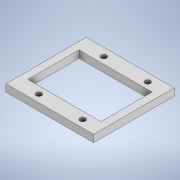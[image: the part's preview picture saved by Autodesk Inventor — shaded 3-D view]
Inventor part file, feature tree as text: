
AUTODESK INVENTOR PART (.ipt)
format: ipt  version: 2022 (Build 260153000, 153)  size: 117,760 bytes
history: native  units: mm
features: extrude x1, sketch x1
ambient origin geometry x8: Origin, YZ Plane, XZ Plane, XY Plane, X Axis, Y Axis, Z Axis, Center Point
bodies: Solid1 (feature_tree)
feature tree (2):
  extrude  "Extrusion1"  Depth=11.0mm
  sketch  "Sketch1"  dims[d0=12.0mm d1=11.0mm d2=5.5mm d3=7.5mm d4=10.0mm d5=7.0mm d6=2.0mm d7=1.0mm d8=0.75mm d9=3.5mm d10=1.0mm d11=20.0mm d13=8.9mm d14=20.0mm d16=6.0mm d19=1.0mm d20=0.0mm]
